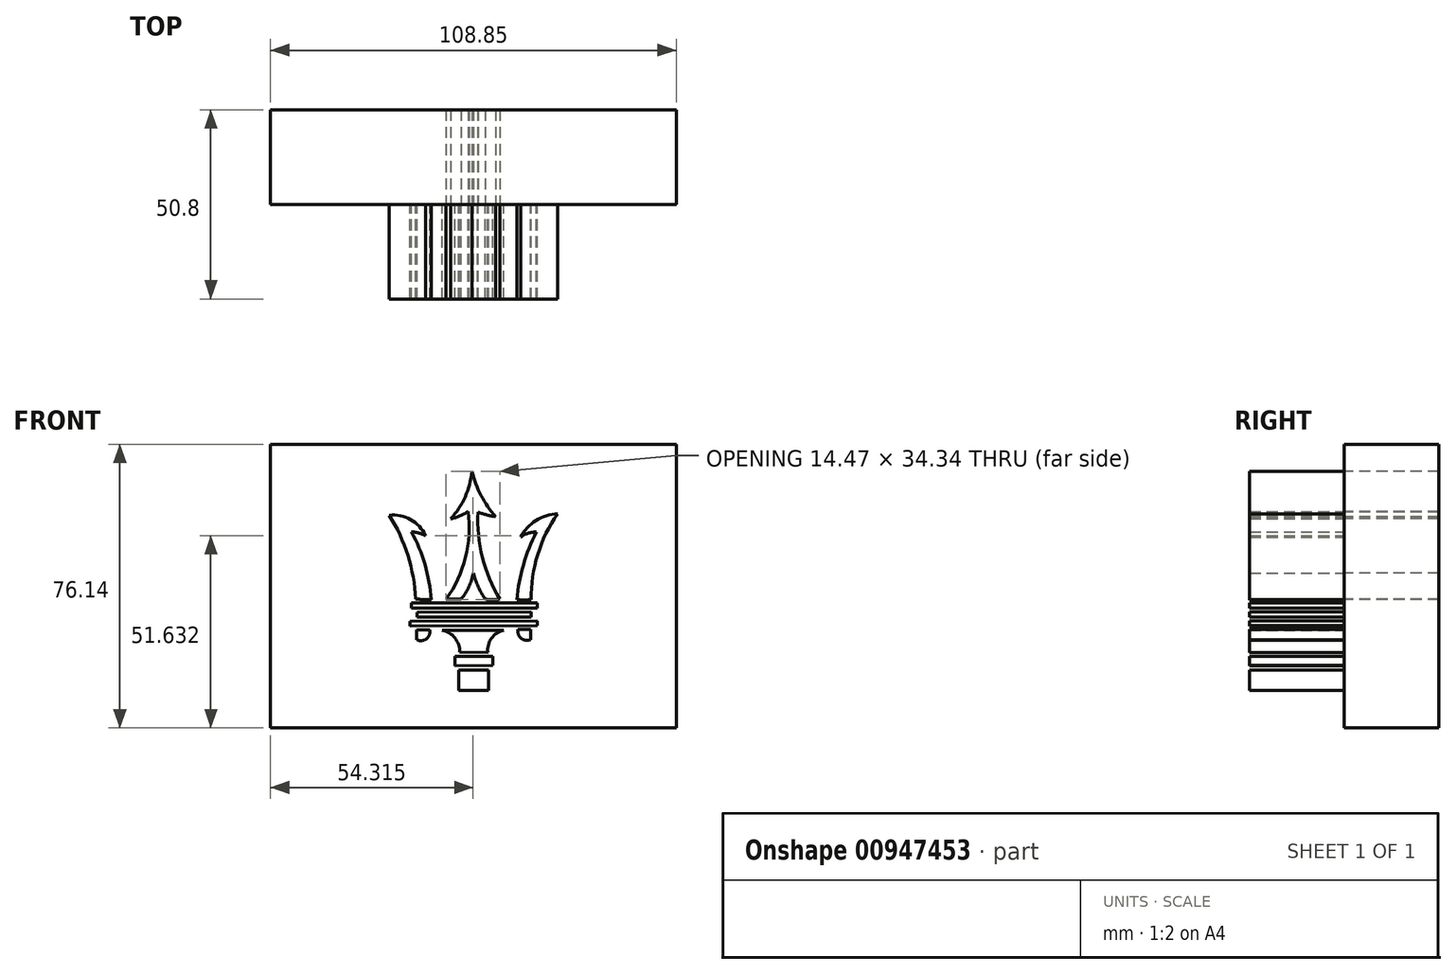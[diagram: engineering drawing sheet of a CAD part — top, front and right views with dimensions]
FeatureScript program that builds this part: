
annotation { "Feature Type Name" : "Feature", "Feature Type Description" : "" }
export const myFeature = defineFeature(function(context is Context, id is Id, definition is map)
    precondition{}
    {
        {
            var Q0;
            Q0=qCreatedBy(makeId("Front.planeOp"),FACE);
            var sketch = newSketch(context, id + "F0", { "sketchPlane" : qUnion([Q0])});
            skArc(sketch, "E0", {"start": v(-15.6, -1.02) * mm, "mid": v(-17.64, 10.72) * mm, "end": v(-22.66, 21.53) * mm});
            skArc(sketch, "E1", {"start": v(-12.93, 16.06) * mm, "mid": v(-16.9, 20.37) * mm, "end": v(-22.66, 21.53) * mm});
            skArc(sketch, "E2", {"start": v(-12.93, 16.06) * mm, "mid": v(-14.75, 16.77) * mm, "end": v(-16.7, 17.06) * mm});
            skArc(sketch, "E3", {"start": v(-11.42, -1.1) * mm, "mid": v(-13.06, 8.27) * mm, "end": v(-16.7, 17.06) * mm});
            skArc(sketch, "E4", {"start": v(-7.41, -1.03) * mm, "mid": v(-2.17, 10.18) * mm, "end": v(-1.46, 22.53) * mm});
            skArc(sketch, "E5", {"start": v(-6.1, 20.59) * mm, "mid": v(-3.69, 21.33) * mm, "end": v(-1.46, 22.53) * mm});
            skArc(sketch, "E6", {"start": v(-6.1, 20.59) * mm, "mid": v(-2.27, 26.46) * mm, "end": v(-0.47, 33.24) * mm});
            skArc(sketch, "E7", {"start": v(-15.6, -1.02) * mm, "mid": v(-13.5, -1.08) * mm, "end": v(-11.42, -1.1) * mm});
            skArc(sketch, "E8", {"start": v(-7.41, -1.03) * mm, "mid": v(-5.4, -1.05) * mm, "end": v(-3.4, -1.03) * mm});
            skArc(sketch, "E9", {"start": v(-3.4, -1.03) * mm, "mid": v(-1.29, 2.28) * mm, "end": v(-0.1, 6.02) * mm});
            skArc(sketch, "E10", {"start": v(-0.1, 6.02) * mm, "mid": v(1.22, 2.37) * mm, "end": v(3.1, -1.03) * mm});
            skArc(sketch, "E11", {"start": v(3.1, -1.03) * mm, "mid": v(5.08, -1.1) * mm, "end": v(7.06, -1.03) * mm});
            skArc(sketch, "E12", {"start": v(1.2, 22.37) * mm, "mid": v(2.34, 10.22) * mm, "end": v(7.06, -1.03) * mm});
            skArc(sketch, "E13", {"start": v(1.2, 22.37) * mm, "mid": v(3.52, 21.6) * mm, "end": v(5.92, 21.14) * mm});
            skArc(sketch, "E14", {"start": v(-0.47, 33.24) * mm, "mid": v(2, 26.82) * mm, "end": v(5.92, 21.14) * mm});
            skArc(sketch, "E15", {"start": v(11.6, -1.1) * mm, "mid": v(13.52, -1.21) * mm, "end": v(15.44, -1.1) * mm});
            skArc(sketch, "E16", {"start": v(22.54, 21.88) * mm, "mid": v(17.18, 10.95) * mm, "end": v(15.44, -1.1) * mm});
            skArc(sketch, "E17", {"start": v(22.54, 21.88) * mm, "mid": v(16.73, 20.12) * mm, "end": v(12.62, 15.65) * mm});
            skArc(sketch, "E18", {"start": v(16.79, 17) * mm, "mid": v(14.59, 16.69) * mm, "end": v(12.62, 15.65) * mm});
            skArc(sketch, "E19", {"start": v(16.79, 17) * mm, "mid": v(13.35, 8.19) * mm, "end": v(11.6, -1.1) * mm});
            skLineSegment(sketch, "E20", {"start": v(-16.76, -3.45) * mm, "end": v(1.4, -3.45) * mm});
            skLineSegment(sketch, "E21", {"start": v(1.4, -3.45) * mm, "end": v(17.03, -3.45) * mm});
            skLineSegment(sketch, "E22", {"start": v(17.03, -3.45) * mm, "end": v(17.03, -2.06) * mm});
            skLineSegment(sketch, "E23", {"start": v(17.03, -2.06) * mm, "end": v(-16.72, -2.06) * mm});
            skLineSegment(sketch, "E24", {"start": v(-16.72, -2.06) * mm, "end": v(-16.76, -3.45) * mm});
            skLineSegment(sketch, "E25", {"start": v(15.48, -4.42) * mm, "end": v(15.48, -5.86) * mm});
            skLineSegment(sketch, "E26", {"start": v(-8.48, -9.32) * mm, "end": v(8.1, -9.32) * mm});
            skLineSegment(sketch, "E27", {"start": v(11.9, -9.15) * mm, "end": v(15.25, -9.15) * mm});
            skLineSegment(sketch, "E28", {"start": v(15.25, -9.15) * mm, "end": v(15.25, -11.85) * mm});
            skLineSegment(sketch, "E29", {"start": v(5.11, -18.76) * mm, "end": v(5.11, -16.35) * mm});
            skLineSegment(sketch, "E30", {"start": v(5.11, -16.35) * mm, "end": v(-5.08, -16.35) * mm});
            skLineSegment(sketch, "E31", {"start": v(-5.08, -16.35) * mm, "end": v(-5.08, -18.88) * mm});
            skLineSegment(sketch, "E32", {"start": v(-5.08, -18.88) * mm, "end": v(5.11, -18.76) * mm});
            skLineSegment(sketch, "E33", {"start": v(3.96, -20.03) * mm, "end": v(3.96, -25.45) * mm});
            skLineSegment(sketch, "E34", {"start": v(3.96, -25.45) * mm, "end": v(-3.99, -25.45) * mm});
            skLineSegment(sketch, "E35", {"start": v(-3.99, -25.45) * mm, "end": v(-3.99, -19.97) * mm});
            skLineSegment(sketch, "E36", {"start": v(-3.99, -19.97) * mm, "end": v(3.96, -20.03) * mm});
            skArc(sketch, "E37", {"start": v(11.9, -9.15) * mm, "mid": v(12.75, -11.52) * mm, "end": v(15.25, -11.85) * mm});
            skLineSegment(sketch, "E38", {"start": v(-15.25, -9.26) * mm, "end": v(-15.25, -11.9) * mm});
            skLineSegment(sketch, "E39", {"start": v(-15.25, -9.26) * mm, "end": v(-11.76, -9.26) * mm});
            skArc(sketch, "E40", {"start": v(-15.25, -11.9) * mm, "mid": v(-12.69, -11.65) * mm, "end": v(-11.76, -9.26) * mm});
            skArc(sketch, "E41", {"start": v(-3.72, -15.27) * mm, "mid": v(-5.01, -11.42) * mm, "end": v(-8.48, -9.32) * mm});
            skArc(sketch, "E42", {"start": v(8.1, -9.32) * mm, "mid": v(4.8, -11.5) * mm, "end": v(3.81, -15.31) * mm});
            skLineSegment(sketch, "E43", {"start": v(15.48, -5.86) * mm, "end": v(-15.22, -5.86) * mm});
            skLineSegment(sketch, "E44", {"start": v(-15.22, -5.86) * mm, "end": v(-15.22, -4.5) * mm});
            skLineSegment(sketch, "E45", {"start": v(-15.22, -4.5) * mm, "end": v(15.48, -4.42) * mm});
            skLineSegment(sketch, "E46", {"start": v(17.11, -8.16) * mm, "end": v(17.11, -6.86) * mm});
            skLineSegment(sketch, "E47", {"start": v(17.11, -6.86) * mm, "end": v(-17.1, -6.94) * mm});
            skLineSegment(sketch, "E48", {"start": v(-17.1, -6.94) * mm, "end": v(-17.1, -8.1) * mm});
            skLineSegment(sketch, "E49", {"start": v(17.11, -8.16) * mm, "end": v(-17.1, -8.24) * mm});
            skLineSegment(sketch, "E50", {"start": v(-17.1, -8.24) * mm, "end": v(-17.1, -8.1) * mm});
            skLineSegment(sketch, "E51", {"start": v(-3.72, -15.27) * mm, "end": v(3.81, -15.31) * mm});
            skSolve(sketch);
        }
        {
            var Q0;
            Q0=makeQuery(id+"F0.imprint","IMPRINT",FACE,{"disambiguationData":[TD([[makeQuery(id+"F0.imprint","IMPRINT",EDGE,{"derivedFrom":sQuery(id+"F0.wireOp",EDGE,"E4")}),-1.0]])]});
            var sketch = newSketch(context, id + "F1", { "sketchPlane" : qUnion([Q0])});
            skLineSegment(sketch, "E52", {"start": v(-54.5, 40.58) * mm, "end": v(-54.5, -35.56) * mm});
            skLineSegment(sketch, "E53", {"start": v(-54.5, -35.56) * mm, "end": v(54.36, -35.56) * mm});
            skLineSegment(sketch, "E54", {"start": v(54.36, -35.56) * mm, "end": v(54.36, 40.58) * mm});
            skLineSegment(sketch, "E55", {"start": v(54.36, 40.58) * mm, "end": v(-54.5, 40.58) * mm});
            skPoint(sketch, "E56.orphan", {"position": v(-54.5, 41.4) * mm});
            skSolve(sketch);
        }
        {
            var Q0;
            Q0 = qSketchRegion(id + "F0", true);
            extrude(context, id + "F2", {"entities" : qUnion([Q0]), "depth" : 25.4 * mm, "offsetDistance" : 25.4 * mm});
        }
        {
            var Q0;
            Q0=makeQuery(id+"F1.imprint","IMPRINT",FACE,{"disambiguationData":[TD([[makeQuery(id+"F1.imprint","IMPRINT",EDGE,{"derivedFrom":sQuery(id+"F1.wireOp",EDGE,"E52")}),1.0]])]});
            extrude(context, id + "F3", {"entities" : qUnion([Q0]), "oppositeDirection" : true, "depth" : 25.4 * mm, "offsetDistance" : 25.4 * mm});
        }
    });
